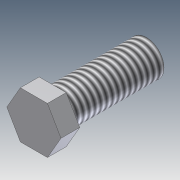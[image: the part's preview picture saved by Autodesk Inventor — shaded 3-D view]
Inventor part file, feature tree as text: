
AUTODESK INVENTOR PART (.ipt)
format: ipt  version: 2012 (Build 160160000, 160)  size: 91,136 bytes
history: native  units: in
note: dims shown in document units (in); Inventor stores cm internally (conversion verified against a paired STEP export)
features: extrude x2, sketch x1, thread x1
ambient origin geometry x8: Origin, YZ Plane, XZ Plane, XY Plane, X Axis, Y Axis, Z Axis, Center Point
bodies: Solid1 (feature_tree)
feature tree (4):
  sketch  "Sketch1"  dims[d10=0.5in d11=1.0in d12=0.0in d13=0.2in d14=0.0in d20=0.375in d21=1.0in d22=0.0in]
  extrude  "Extrusion1"  Depth=1.0in TaperAngle=0.0deg
  extrude  "Extrusion2"  Depth=0.2in TaperAngle=0.0deg
  thread  "Thread2"  [1 undecoded]
note: 1 required parameter value undecoded (feature->parameter linkage not recoverable at this tier; creation-order binding heuristic only, values carry confidence <= 0.55)
